# Revit family: Door_FTS RD_The Sliding Door Company_2-Panel Double Track (Ramped)
name_source: partatom
category: Doors
units: mm (PartAtom-declared; Revit-internal decimal feet)

## family parameters
Always vertical = Yes
Cut with Voids When Loaded = No
Host = Wall
OmniClass Number = 23.30.10.00
OmniClass Title = Doors
Room Calculation Point = No
Shared = No

## types (1)
- FTS Room Divider - 2 Panel 2 Track (Ramped) - AB/BA
    1 1/2" Frame (No Support Dividers) = Max. H=108 in., Max. W=97 in. (50 in. panel width)
    3" Frame (No Support Dividers) = Max. H=122 in., Max. W=101 in. (52 in. panel width)
    Analytic Construction = <None>
    Configuration = AB/BA Configuration
    Construction Type = Top Mounted, Ramped Bottom Track
    Description = 2 Panel System with Double Track (Ramped)
    Finished Opening Height = 122"
    Finished Opening Width = 101"
    Function = Interior
    Glass Thickness = Available in: 5mm Tempered, 7mm,10mm,11mm Laminated Glass
    Height = 122"
    Limitations = Panel Width x System Height cannot exceed 7,400 square inches
    Manufacturer = The Sliding Door Company
    Model = FTS Room Divider - Full Height System
    Panel Height = 119 3/4"
    Panel Width 1 1/2" Frame = 51 1/4"
    Panel Width 3" Frame = 52"
    Rough Height = 122 5/8"
    Rough Width = 102 1/4"
    Stile and Rail = 1 1/2"
    Thickness = 1 1/4"
    URL = https://www.slidingdoorco.com
    Wall Closure = By host
    Width = 101"

## geometry (parser evidence)
native form markers: Blend x3, Sweep x5
no freeform markers — native parametric forms only
